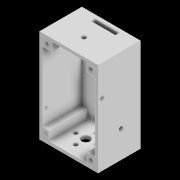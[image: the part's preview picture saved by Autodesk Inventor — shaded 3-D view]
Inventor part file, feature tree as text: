
AUTODESK INVENTOR PART (.ipt)
format: ipt  version: 2020 (Build 240168000, 168)  size: 227,328 bytes
history: native  units: mm
features: sketch x10, hole x6, extrude x4, projected_geometry x4, pattern_circular x1, fillet x1
ambient origin geometry x8: Origin, YZ Plane, XZ Plane, XY Plane, X Axis, Y Axis, Z Axis, Center Point
bodies: Solid1 (feature_tree)
feature tree (26):
  extrude  "Extrusion1"  Depth=79.0mm
  extrude  "Extrusion2"  Depth=2.5mm
  hole  "Hole1"  [1 undecoded]
  hole  "Hole2"  [1 undecoded]
  pattern_circular  "Circular Pattern1"  Count=4 Angle=360.0deg
  hole  "Hole3"  [1 undecoded]
  fillet  "Fillet3"  Radius=30.48mm
  hole  "Hole4"  [1 undecoded]
  extrude  "Extrusion3"  Depth=2.0mm
  hole  "Hole5"  [1 undecoded]
  hole  "Hole6"  [1 undecoded]
  extrude  "Extrusion4"  Depth=76.5mm
  sketch  "Sketch1"  dims[d0=49.5mm d1=79.0mm]
  sketch  "Sketch2"  dims[d2=35.867mm d3=0.0mm d4=2.5mm]
  sketch  "Sketch3"  dims[d5=2.5mm d6=2.5mm]
  projected_geometry  "Projected Loop1"
  sketch  "Sketch4"  dims[d7=2.5mm d8=32.367mm d9=0.0mm]
  projected_geometry  "Projected Loop2"
  sketch  "Sketch5"  dims[d12=17.367mm]
  sketch  "Sketch6"  dims[d13=7.1mm d14=6.0mm d15=4.0mm d16=2.0mm d17=90.0deg d18=8.0mm d19=20.594885mm]
  sketch  "Sketch7"  dims[d20=8.5mm]
  sketch  "Sketch8"  dims[d21=3.3mm d22=6.0mm d23=4.0mm d24=2.0mm d25=90.0deg d26=8.0mm d27=20.594885mm d28=40.0mm d29=360.0deg]
  projected_geometry  "Projected Loop3"
  sketch  "Sketch9"  dims[d31=21.75mm d32=2.986mm d33=30.48mm]
  sketch  "Sketch10"  dims[d34=22.86mm d35=22.952888mm d36=2.184mm d37=6.0mm d38=4.0mm d39=2.0mm d40=90.0deg d41=8.0mm d42=20.594885mm d43=2.0mm d44=30.0mm d47=26.0mm d48=3.0mm d49=6.0mm d50=4.0mm d51=2.0mm d52=90.0deg d53=8.0mm d54=20.594885mm d55=3.2mm d56=16.0mm d57=10.0mm d58=8.0mm d59=10.0mm d60=10.0mm d61=10.0mm d62=10.0mm d63=10.0mm d64=10.0mm d66=28.5mm d67=0.0mm d68=3.3mm d69=6.0mm d70=4.0mm d71=2.0mm d72=90.0deg d73=8.0mm d74=20.594885mm d75=14.228mm d76=3.3mm d77=6.0mm d78=4.0mm d79=2.0mm d80=90.0deg d81=8.0mm d82=20.594885mm d83=20.0mm d84=3.0mm d85=76.5mm d86=0.0mm d87=13.419mm]
  projected_geometry  "Projected Loop4"
note: 6 required parameter values undecoded (feature->parameter linkage not recoverable at this tier; creation-order binding heuristic only, values carry confidence <= 0.55)
